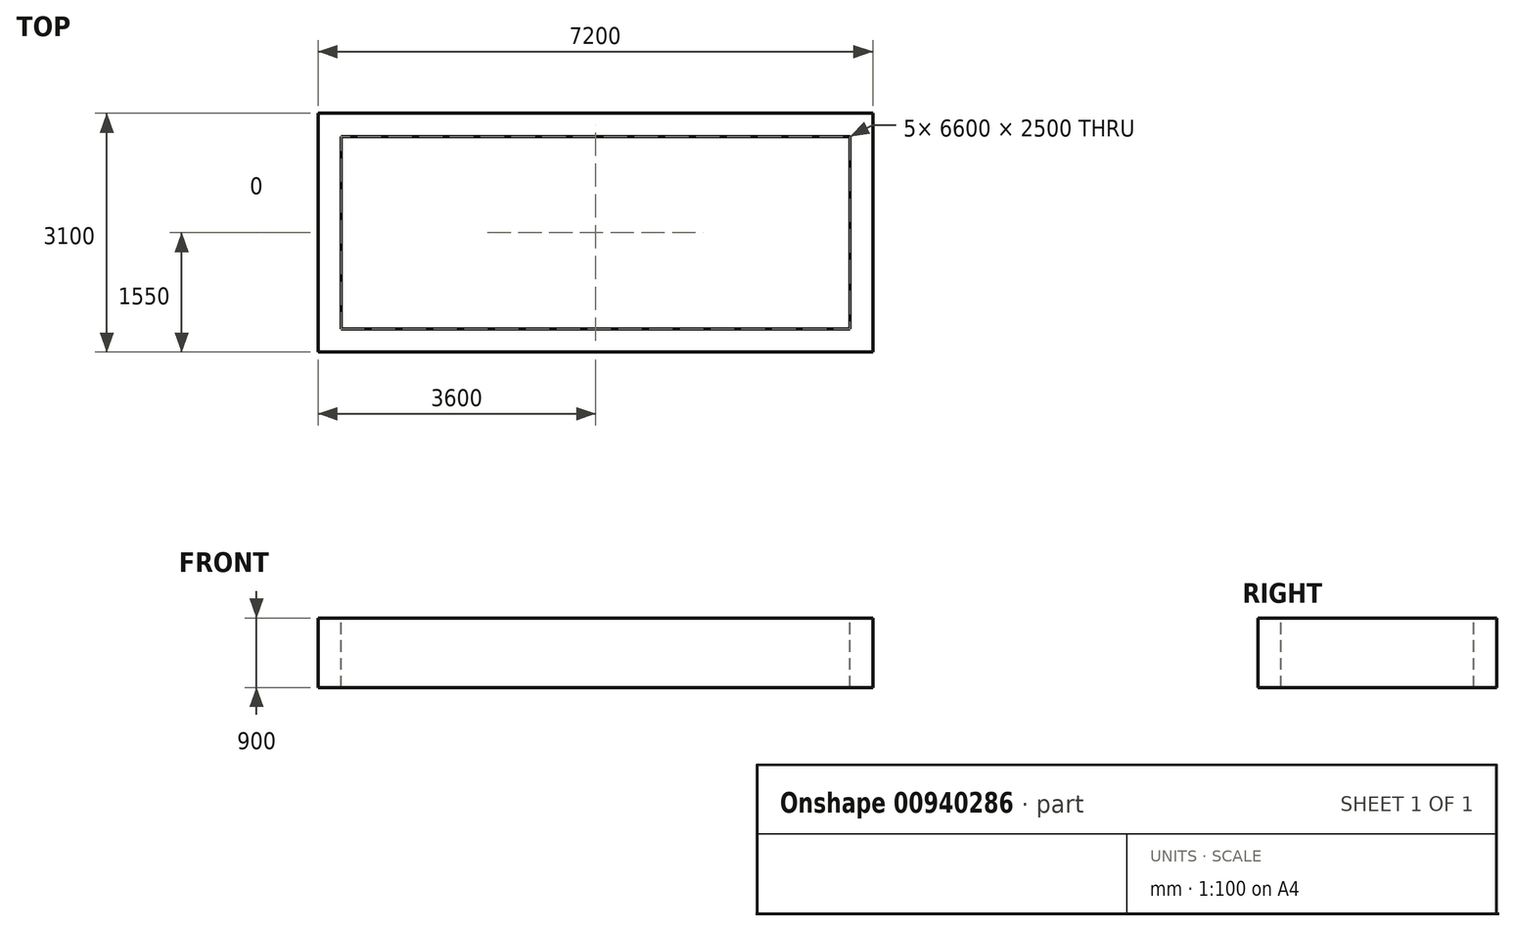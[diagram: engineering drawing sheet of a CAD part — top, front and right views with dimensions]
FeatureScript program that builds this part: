
annotation { "Feature Type Name" : "Feature", "Feature Type Description" : "" }
export const myFeature = defineFeature(function(context is Context, id is Id, definition is map)
    precondition{}
    {
        {
            var Q0;
            Q0=qCreatedBy(makeId("Top.planeOp"),FACE);
            var sketch = newSketch(context, id + "F0", { "sketchPlane" : qUnion([Q0])});
            skLineSegment(sketch, "E0.bottom", {"start": v(-3600, 1550) * mm, "end": v(3600, 1550) * mm});
            skLineSegment(sketch, "E0.top", {"start": v(-3600, -1550) * mm, "end": v(3600, -1550) * mm});
            skLineSegment(sketch, "E0.left", {"start": v(-3600, 1550) * mm, "end": v(-3600, -1550) * mm});
            skLineSegment(sketch, "E0.right", {"start": v(3600, 1550) * mm, "end": v(3600, -1550) * mm});
            skLineSegment(sketch, "E1.0", {"start": v(-3300, 1250) * mm, "end": v(3300, 1250) * mm});
            skLineSegment(sketch, "E1.1", {"start": v(-3300, 1250) * mm, "end": v(-3300, -1250) * mm});
            skLineSegment(sketch, "E1.2", {"start": v(-3300, -1250) * mm, "end": v(3300, -1250) * mm});
            skLineSegment(sketch, "E1.3", {"start": v(3300, 1250) * mm, "end": v(3300, -1250) * mm});
            skSolve(sketch);
        }
        {
            var Q0;
            Q0 = qSketchRegion(id + "F0", true);
            extrude(context, id + "F1", {"entities" : qUnion([Q0]), "oppositeDirection" : true, "depth" : 900 * mm, "offsetDistance" : 25 * mm});
        }
    });
